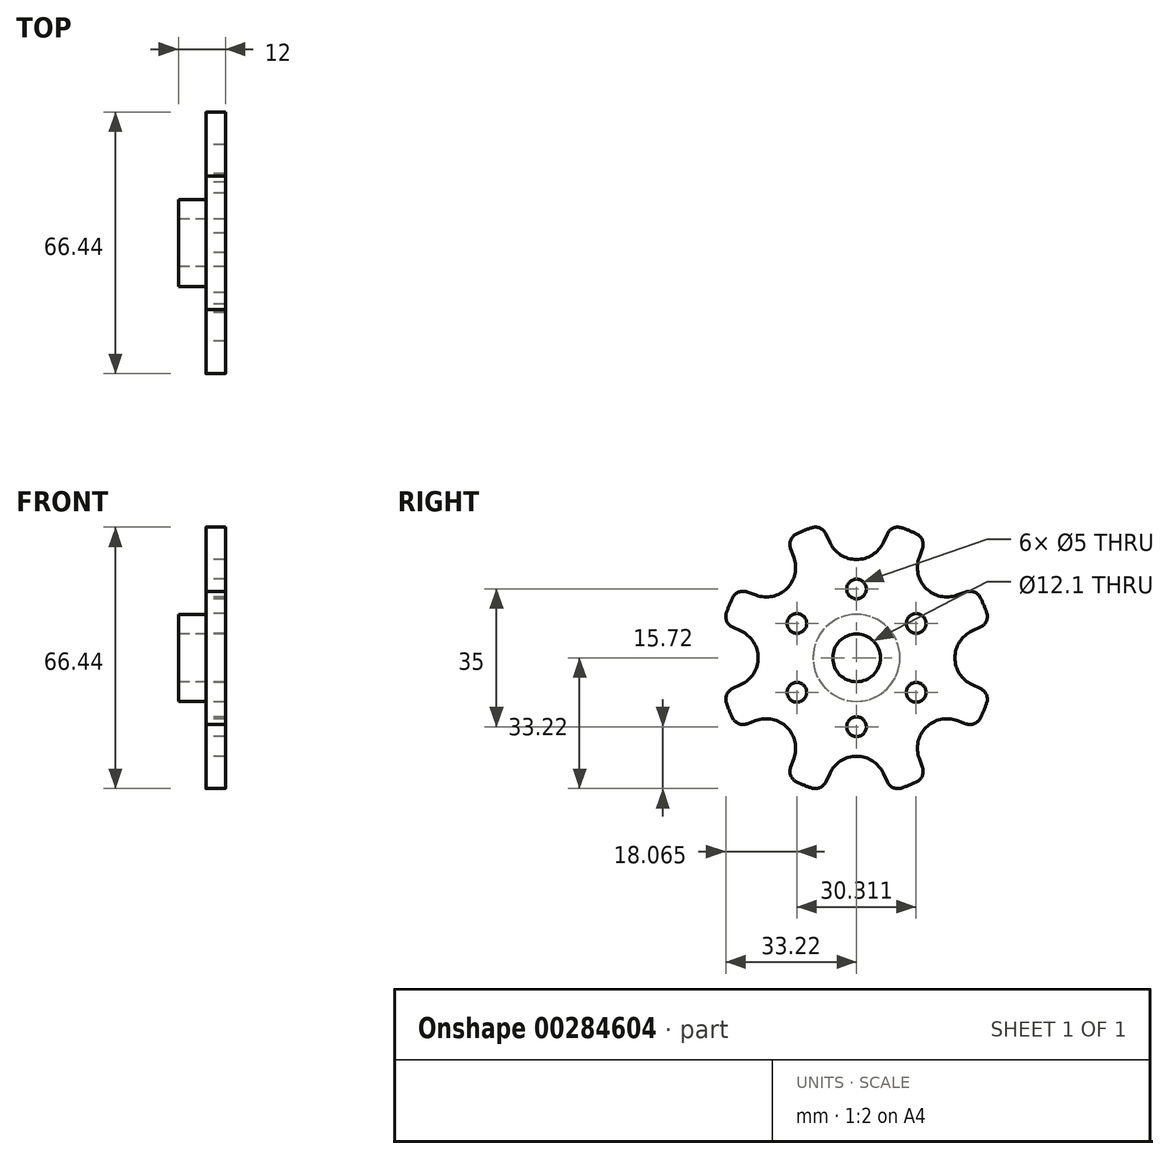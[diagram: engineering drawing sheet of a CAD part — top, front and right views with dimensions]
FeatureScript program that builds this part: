
annotation { "Feature Type Name" : "Feature", "Feature Type Description" : "" }
export const myFeature = defineFeature(function(context is Context, id is Id, definition is map)
    precondition{}
    {
        {
            var Q0;
            Q0=qCreatedBy(makeId("Right.planeOp"),FACE);
            var sketch = newSketch(context, id + "F0", { "sketchPlane" : qUnion([Q0])});
            skCircle(sketch, "E0", {"center": v(0, 0) * mm, "radius": 25 * mm, "construction": true});
            skArc(sketch, "E1", {"start": v(-8.9, 33.85) * mm, "mid": v(0, -35) * mm, "end": v(8.9, 33.85) * mm, "construction": true});
            skLineSegment(sketch, "E2", {"start": v(0, 0) * mm, "end": v(0, 35) * mm, "construction": true});
            skLineSegment(sketch, "E3.1.0", {"start": v(0, 0) * mm, "end": v(-13.4, 32.34) * mm, "construction": true});
            skLineSegment(sketch, "E3.2.0", {"start": v(0, 0) * mm, "end": v(-17.68, 17.68) * mm, "construction": true});
            skLineSegment(sketch, "E3.3.0", {"start": v(0, 0) * mm, "end": v(-23.1, 9.57) * mm, "construction": true});
            skLineSegment(sketch, "E3.4.0", {"start": v(0, 0) * mm, "end": v(-25, 0) * mm, "construction": true});
            skLineSegment(sketch, "E3.5.0", {"start": v(0, 0) * mm, "end": v(-23.1, -9.57) * mm, "construction": true});
            skLineSegment(sketch, "E3.6.0", {"start": v(0, 0) * mm, "end": v(-17.68, -17.68) * mm, "construction": true});
            skLineSegment(sketch, "E3.7.0", {"start": v(0, 0) * mm, "end": v(-9.57, -23.1) * mm, "construction": true});
            skLineSegment(sketch, "E3.8.0", {"start": v(0, 0) * mm, "end": v(0, -25) * mm, "construction": true});
            skLineSegment(sketch, "E3.9.0", {"start": v(0, 0) * mm, "end": v(9.57, -23.1) * mm, "construction": true});
            skLineSegment(sketch, "E3.10.0", {"start": v(0, 0) * mm, "end": v(17.68, -17.68) * mm, "construction": true});
            skLineSegment(sketch, "E3.11.0", {"start": v(0, 0) * mm, "end": v(23.1, -9.57) * mm, "construction": true});
            skLineSegment(sketch, "E3.12.0", {"start": v(0, 0) * mm, "end": v(25, 0) * mm, "construction": true});
            skLineSegment(sketch, "E3.13.0", {"start": v(0, 0) * mm, "end": v(23.1, 9.57) * mm, "construction": true});
            skLineSegment(sketch, "E3.14.0", {"start": v(0, 0) * mm, "end": v(17.68, 17.68) * mm, "construction": true});
            skLineSegment(sketch, "E3.15.0", {"start": v(0, 0) * mm, "end": v(13.4, 32.34) * mm, "construction": true});
            skPoint(sketch, "E4.orphan", {"position": v(0, 25) * mm});
            skPoint(sketch, "E5.orphan", {"position": v(-9.57, 23.1) * mm});
            skPoint(sketch, "E6.orphan", {"position": v(9.57, 23.1) * mm});
            skArc(sketch, "E7", {"start": v(-6.8, 29.33) * mm, "mid": v(0, 25) * mm, "end": v(6.8, 29.33) * mm});
            skLineSegment(sketch, "E8", {"start": v(6.8, 29.33) * mm, "end": v(0, 29.33) * mm, "construction": true});
            skLineSegment(sketch, "E9", {"start": v(-6.8, 29.33) * mm, "end": v(0, 29.33) * mm, "construction": true});
            skLineSegment(sketch, "E10", {"start": v(-6.8, 29.33) * mm, "end": v(-7.8, 31.49) * mm});
            skLineSegment(sketch, "E11", {"start": v(6.8, 29.33) * mm, "end": v(7.8, 31.49) * mm});
            skLineSegment(sketch, "E12.1.0", {"start": v(-15.93, 25.55) * mm, "end": v(-16.75, 27.78) * mm});
            skArc(sketch, "E12.1.1", {"start": v(-25.55, 15.93) * mm, "mid": v(-17.68, 17.68) * mm, "end": v(-15.93, 25.55) * mm});
            skLineSegment(sketch, "E12.1.2", {"start": v(-25.55, 15.93) * mm, "end": v(-27.78, 16.75) * mm});
            skLineSegment(sketch, "E12.2.0", {"start": v(-29.33, 6.8) * mm, "end": v(-31.49, 7.8) * mm});
            skArc(sketch, "E12.2.1", {"start": v(-29.33, -6.8) * mm, "mid": v(-25, 0) * mm, "end": v(-29.33, 6.8) * mm});
            skLineSegment(sketch, "E12.2.2", {"start": v(-29.33, -6.8) * mm, "end": v(-31.49, -7.8) * mm});
            skLineSegment(sketch, "E12.3.0", {"start": v(-25.55, -15.93) * mm, "end": v(-27.78, -16.75) * mm});
            skArc(sketch, "E12.3.1", {"start": v(-15.93, -25.55) * mm, "mid": v(-17.68, -17.68) * mm, "end": v(-25.55, -15.93) * mm});
            skLineSegment(sketch, "E12.3.2", {"start": v(-15.93, -25.55) * mm, "end": v(-16.75, -27.78) * mm});
            skLineSegment(sketch, "E12.4.0", {"start": v(-6.8, -29.33) * mm, "end": v(-7.8, -31.49) * mm});
            skArc(sketch, "E12.4.1", {"start": v(6.8, -29.33) * mm, "mid": v(0, -25) * mm, "end": v(-6.8, -29.33) * mm});
            skLineSegment(sketch, "E12.4.2", {"start": v(6.8, -29.33) * mm, "end": v(7.8, -31.49) * mm});
            skLineSegment(sketch, "E12.5.0", {"start": v(15.93, -25.55) * mm, "end": v(16.75, -27.78) * mm});
            skArc(sketch, "E12.5.1", {"start": v(25.55, -15.93) * mm, "mid": v(17.68, -17.68) * mm, "end": v(15.93, -25.55) * mm});
            skLineSegment(sketch, "E12.5.2", {"start": v(25.55, -15.93) * mm, "end": v(27.78, -16.75) * mm});
            skLineSegment(sketch, "E12.6.0", {"start": v(29.33, -6.8) * mm, "end": v(31.49, -7.8) * mm});
            skArc(sketch, "E12.6.1", {"start": v(29.33, 6.8) * mm, "mid": v(25, 0) * mm, "end": v(29.33, -6.8) * mm});
            skLineSegment(sketch, "E12.6.2", {"start": v(29.33, 6.8) * mm, "end": v(31.49, 7.8) * mm});
            skLineSegment(sketch, "E12.7.0", {"start": v(25.55, 15.93) * mm, "end": v(27.78, 16.75) * mm});
            skArc(sketch, "E12.7.1", {"start": v(15.93, 25.55) * mm, "mid": v(17.68, 17.68) * mm, "end": v(25.55, 15.93) * mm});
            skLineSegment(sketch, "E12.7.2", {"start": v(15.93, 25.55) * mm, "end": v(16.75, 27.78) * mm});
            skArc(sketch, "E13", {"start": v(-11.5, 33.05) * mm, "mid": v(-13.4, 32.34) * mm, "end": v(-15.23, 31.51) * mm});
            skArc(sketch, "E14", {"start": v(15.23, 31.51) * mm, "mid": v(13.4, 32.34) * mm, "end": v(11.5, 33.05) * mm});
            skLineSegment(sketch, "E15.2.0", {"start": v(0, 0) * mm, "end": v(-24.75, 24.75) * mm, "construction": true});
            skLineSegment(sketch, "E15.3.0", {"start": v(0, 0) * mm, "end": v(-32.34, 13.4) * mm, "construction": true});
            skLineSegment(sketch, "E15.4.0", {"start": v(0, 0) * mm, "end": v(-35, 0) * mm, "construction": true});
            skLineSegment(sketch, "E15.5.0", {"start": v(0, 0) * mm, "end": v(-32.34, -13.4) * mm, "construction": true});
            skLineSegment(sketch, "E15.6.0", {"start": v(0, 0) * mm, "end": v(-24.75, -24.75) * mm, "construction": true});
            skLineSegment(sketch, "E15.7.0", {"start": v(0, 0) * mm, "end": v(-13.4, -32.34) * mm, "construction": true});
            skLineSegment(sketch, "E16.1.8.0", {"start": v(0, 0) * mm, "end": v(0, -35) * mm, "construction": true});
            skLineSegment(sketch, "E16.1.9.0", {"start": v(0, 0) * mm, "end": v(13.4, -32.34) * mm, "construction": true});
            skLineSegment(sketch, "E16.1.10.0", {"start": v(0, 0) * mm, "end": v(24.75, -24.75) * mm, "construction": true});
            skLineSegment(sketch, "E16.1.11.0", {"start": v(0, 0) * mm, "end": v(32.34, -13.4) * mm, "construction": true});
            skLineSegment(sketch, "E16.1.12.0", {"start": v(0, 0) * mm, "end": v(35, 0) * mm, "construction": true});
            skLineSegment(sketch, "E16.1.13.0", {"start": v(0, 0) * mm, "end": v(32.34, 13.4) * mm, "construction": true});
            skLineSegment(sketch, "E16.1.14.0", {"start": v(0, 0) * mm, "end": v(24.75, 24.75) * mm, "construction": true});
            skArc(sketch, "E17", {"start": v(33.05, 11.5) * mm, "mid": v(32.34, 13.4) * mm, "end": v(31.51, 15.23) * mm});
            skArc(sketch, "E18", {"start": v(31.51, -15.23) * mm, "mid": v(32.34, -13.4) * mm, "end": v(33.05, -11.5) * mm});
            skArc(sketch, "E19", {"start": v(11.5, -33.05) * mm, "mid": v(13.4, -32.34) * mm, "end": v(15.23, -31.51) * mm});
            skArc(sketch, "E20", {"start": v(-15.23, -31.51) * mm, "mid": v(-13.4, -32.34) * mm, "end": v(-11.5, -33.05) * mm});
            skArc(sketch, "E21", {"start": v(-33.05, -11.5) * mm, "mid": v(-32.34, -13.4) * mm, "end": v(-31.51, -15.23) * mm});
            skArc(sketch, "E22", {"start": v(-31.51, 15.23) * mm, "mid": v(-32.34, 13.4) * mm, "end": v(-33.05, 11.5) * mm});
            skPoint(sketch, "E23.visualSharp", {"position": v(-8.9, 33.85) * mm});
            skArc(sketch, "E23.filletArc", {"start": v(-7.8, 31.49) * mm, "mid": v(-9.36, 32.98) * mm, "end": v(-11.5, 33.05) * mm});
            skPoint(sketch, "E24.visualSharp", {"position": v(8.9, 33.85) * mm});
            skArc(sketch, "E24.filletArc", {"start": v(11.5, 33.05) * mm, "mid": v(9.36, 32.98) * mm, "end": v(7.8, 31.49) * mm});
            skPoint(sketch, "E25.visualSharp", {"position": v(17.64, 30.23) * mm});
            skArc(sketch, "E25.filletArc", {"start": v(16.75, 27.78) * mm, "mid": v(16.7, 29.94) * mm, "end": v(15.23, 31.51) * mm});
            skPoint(sketch, "E26.visualSharp", {"position": v(30.23, 17.64) * mm});
            skArc(sketch, "E26.filletArc", {"start": v(31.51, 15.23) * mm, "mid": v(29.94, 16.7) * mm, "end": v(27.78, 16.75) * mm});
            skPoint(sketch, "E27.visualSharp", {"position": v(33.85, 8.9) * mm});
            skArc(sketch, "E27.filletArc", {"start": v(31.49, 7.8) * mm, "mid": v(32.98, 9.36) * mm, "end": v(33.05, 11.5) * mm});
            skPoint(sketch, "E28.visualSharp", {"position": v(33.85, -8.9) * mm});
            skArc(sketch, "E28.filletArc", {"start": v(33.05, -11.5) * mm, "mid": v(32.98, -9.36) * mm, "end": v(31.49, -7.8) * mm});
            skPoint(sketch, "E29.visualSharp", {"position": v(30.23, -17.64) * mm});
            skArc(sketch, "E29.filletArc", {"start": v(27.78, -16.75) * mm, "mid": v(29.94, -16.7) * mm, "end": v(31.51, -15.23) * mm});
            skPoint(sketch, "E30.visualSharp", {"position": v(17.64, -30.23) * mm});
            skArc(sketch, "E30.filletArc", {"start": v(15.23, -31.51) * mm, "mid": v(16.7, -29.94) * mm, "end": v(16.75, -27.78) * mm});
            skPoint(sketch, "E31.visualSharp", {"position": v(8.9, -33.85) * mm});
            skArc(sketch, "E31.filletArc", {"start": v(7.8, -31.49) * mm, "mid": v(9.36, -32.98) * mm, "end": v(11.5, -33.05) * mm});
            skPoint(sketch, "E32.visualSharp", {"position": v(-8.9, -33.85) * mm});
            skArc(sketch, "E32.filletArc", {"start": v(-11.5, -33.05) * mm, "mid": v(-9.36, -32.98) * mm, "end": v(-7.8, -31.49) * mm});
            skPoint(sketch, "E33.visualSharp", {"position": v(-17.64, -30.23) * mm});
            skArc(sketch, "E33.filletArc", {"start": v(-16.75, -27.78) * mm, "mid": v(-16.7, -29.94) * mm, "end": v(-15.23, -31.51) * mm});
            skPoint(sketch, "E34.visualSharp", {"position": v(-30.23, -17.64) * mm});
            skArc(sketch, "E34.filletArc", {"start": v(-31.51, -15.23) * mm, "mid": v(-29.94, -16.7) * mm, "end": v(-27.78, -16.75) * mm});
            skPoint(sketch, "E35.visualSharp", {"position": v(-33.85, -8.9) * mm});
            skArc(sketch, "E35.filletArc", {"start": v(-31.49, -7.8) * mm, "mid": v(-32.98, -9.36) * mm, "end": v(-33.05, -11.5) * mm});
            skPoint(sketch, "E36.visualSharp", {"position": v(-33.85, 8.9) * mm});
            skArc(sketch, "E36.filletArc", {"start": v(-33.05, 11.5) * mm, "mid": v(-32.98, 9.36) * mm, "end": v(-31.49, 7.8) * mm});
            skPoint(sketch, "E37.visualSharp", {"position": v(-30.23, 17.64) * mm});
            skArc(sketch, "E37.filletArc", {"start": v(-27.78, 16.75) * mm, "mid": v(-29.94, 16.7) * mm, "end": v(-31.51, 15.23) * mm});
            skPoint(sketch, "E38.visualSharp", {"position": v(-17.64, 30.23) * mm});
            skArc(sketch, "E38.filletArc", {"start": v(-15.23, 31.51) * mm, "mid": v(-16.7, 29.94) * mm, "end": v(-16.75, 27.78) * mm});
            skCircle(sketch, "E39", {"center": v(0, 0) * mm, "radius": 6.05 * mm});
            skCircle(sketch, "E40", {"center": v(0, 17.5) * mm, "radius": 2.5 * mm});
            skCircle(sketch, "E41.1.0", {"center": v(-15.16, 8.75) * mm, "radius": 2.5 * mm});
            skCircle(sketch, "E41.2.0", {"center": v(-15.16, -8.75) * mm, "radius": 2.5 * mm});
            skCircle(sketch, "E41.3.0", {"center": v(0, -17.5) * mm, "radius": 2.5 * mm});
            skCircle(sketch, "E41.4.0", {"center": v(15.16, -8.75) * mm, "radius": 2.5 * mm});
            skCircle(sketch, "E41.5.0", {"center": v(15.16, 8.75) * mm, "radius": 2.5 * mm});
            skSolve(sketch);
        }
        {
            var Q0;
            Q0=qSketchRegion(id+"F0",true);
            extrude(context, id + "F1", {"entities" : qUnion([Q0]), "depth" : 5 * mm});
        }
        {
            var Q0;
            Q0=qCreatedBy(makeId("Front.planeOp"),FACE);
            var sketch = newSketch(context, id + "F2", { "sketchPlane" : qUnion([Q0])});
            skLineSegment(sketch, "E42", {"start": v(0, 6.05) * mm, "end": v(0, 11.05) * mm});
            skLineSegment(sketch, "E43", {"start": v(0, 11.05) * mm, "end": v(-7, 11.05) * mm});
            skLineSegment(sketch, "E44", {"start": v(-7, 11.05) * mm, "end": v(-7, 6.05) * mm});
            skLineSegment(sketch, "E45", {"start": v(-7, 6.05) * mm, "end": v(0, 6.05) * mm});
            skLineSegment(sketch, "E46", {"start": v(-19.9, 0) * mm, "end": v(39.42, 0) * mm, "construction": true});
            skSolve(sketch);
        }
        {
            var Q0;
            Q0 = qSketchRegion(id + "F2", true);
            var Q1;
            Q1=sQuery(id+"F2.wireOp",EDGE,"E46");
            revolve(context, id + "F3", {"operationType" : NewBodyOperationType.ADD, "entities" : qUnion([Q0]), "axis" : qUnion([Q1]), "revolveType" : RevolveType.FULL});
        }
    });
